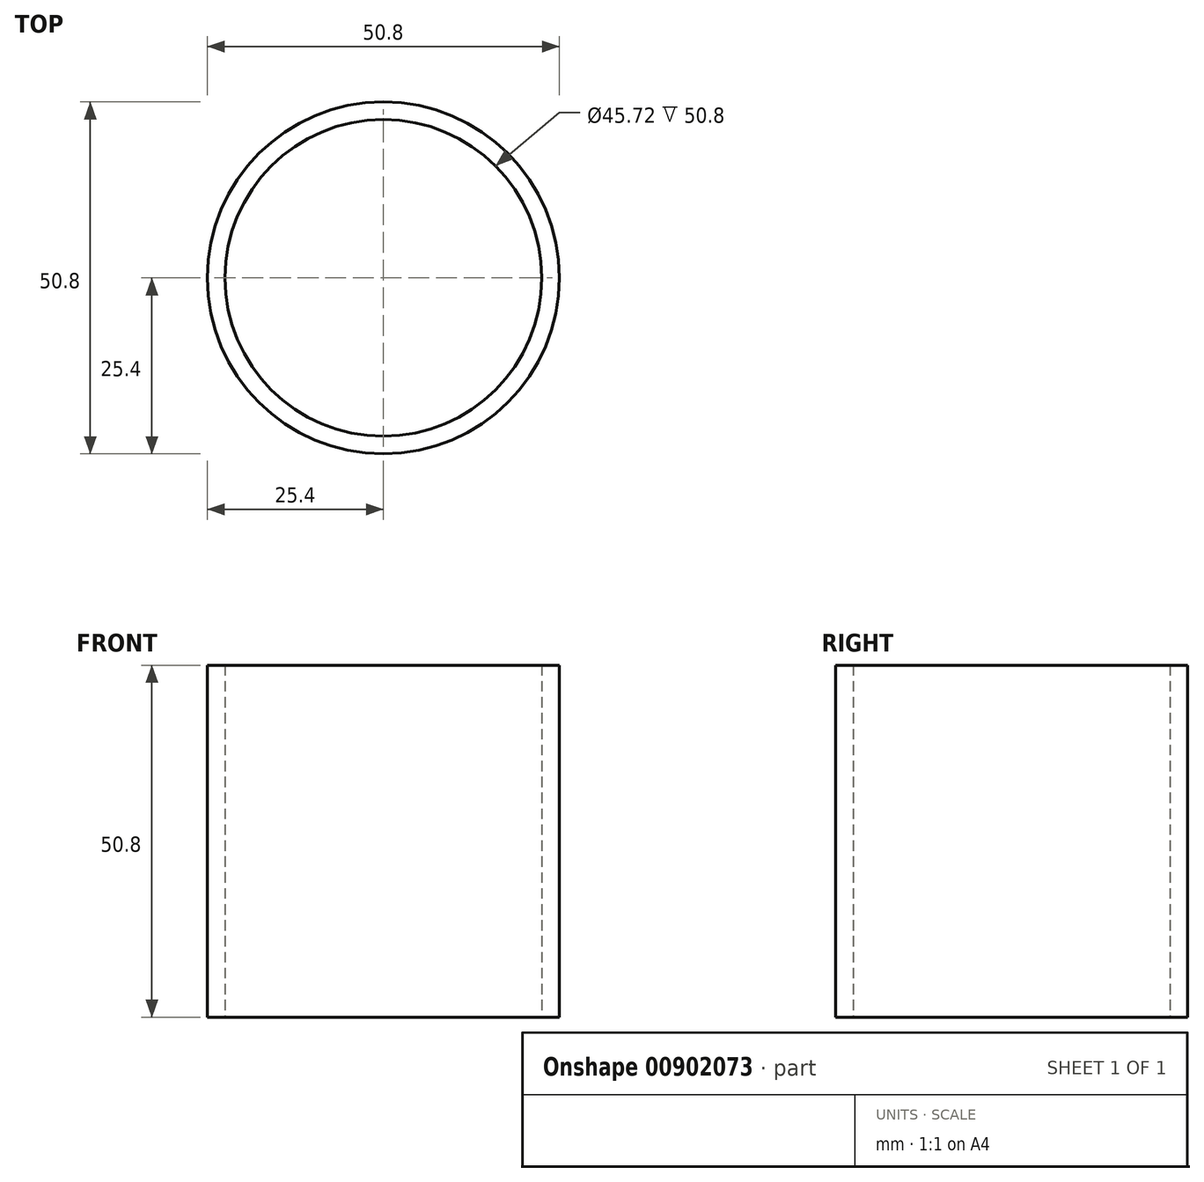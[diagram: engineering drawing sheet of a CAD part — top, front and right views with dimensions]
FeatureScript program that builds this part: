
annotation { "Feature Type Name" : "Feature", "Feature Type Description" : "" }
export const myFeature = defineFeature(function(context is Context, id is Id, definition is map)
    precondition{}
    {
        {
            var Q0;
            Q0=qCreatedBy(makeId("Top.planeOp"),FACE);
            var sketch = newSketch(context, id + "F0", { "sketchPlane" : qUnion([Q0])});
            skCircle(sketch, "E0", {"center": v(0, 0) * mm, "radius": 25.4 * mm});
            skCircle(sketch, "E1", {"center": v(0, 0) * mm, "radius": 22.86 * mm});
            skSolve(sketch);
        }
        {
            var Q0;
            Q0=makeQuery(id+"F0.imprint","IMPRINT",FACE,{"disambiguationData":[TD([[makeQuery(id+"F0.imprint","IMPRINT",EDGE,{"derivedFrom":sQuery(id+"F0.wireOp",EDGE,"E0")}),1.0]])]});
            extrude(context, id + "F1", {"entities" : qUnion([Q0]), "depth" : 50.8 * mm, "offsetDistance" : 25.4 * mm});
        }
    });
